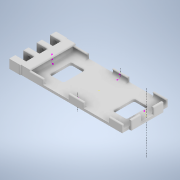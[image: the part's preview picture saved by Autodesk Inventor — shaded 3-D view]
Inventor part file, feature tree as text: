
AUTODESK INVENTOR PART (.ipt)
format: ipt  version: 2020 (Build 240168000, 168)  size: 727,040 bytes
history: native  units: mm
features: projected_geometry x18, sketch x14, extrude x12, other x3
ambient origin geometry x8: Origin, YZ Plane, XZ Plane, XY Plane, X Axis, Y Axis, Z Axis, Center Point
bodies: Solid1 (feature_tree)
feature tree (47):
  other  "Part9.1.ipt"
  extrude  "Extrusion1"  Depth=0.405517mm TaperAngle=0.0deg
  extrude  "Extrusion2"  Depth=15.5mm TaperAngle=0.0deg
  extrude  "Extrusion3"  Depth=20.0mm TaperAngle=0.0deg
  extrude  "Extrusion4"  Depth=40.0mm
  extrude  "Extrusion5"  Depth=12.0mm
  sketch  "Sketch10"  dims[d70=5.0mm d71=8.75mm]
  extrude  "Extrusion8"  Depth=8.75mm
  sketch  "Sketch22"  dims[d72=1.0mm d73=0.0mm d74=1.0mm d75=0.0mm]
  sketch  "Sketch23"  dims[d76=97.5mm d77=0.0mm d88=97.5mm d89=0.0mm]
  extrude  "Extrusion15"  Depth=1.0mm TaperAngle=0.0deg
  sketch  "Sketch27"  dims[d92=8.3mm d93=8.3mm]
  extrude  "Extrusion16"  Depth=97.5mm TaperAngle=0.0deg
  extrude  "Extrusion17"  Depth=17.25mm
  extrude  "Extrusion18"  Depth=8.3mm
  extrude  "Extrusion19"  Depth=12.8mm
  extrude  "Extrusion20"  Depth=9.591003mm
  other  "Solid2::Part9.1.ipt"
  other  "TaggingFeature1"
  sketch  "Sketch1"  dims[d0=0.405517mm d1=50.68mm d2=0.0mm]
  sketch  "Sketch3"  dims[d7=8.5mm d8=0.0mm d9=15.5mm d10=0.0mm]
  projected_geometry  "Projected Loop1"
  sketch  "Sketch5"  dims[d15=15.5mm d16=0.0mm d17=20.0mm d18=0.0mm]
  sketch  "Sketch6"  dims[d36=141.75mm d37=0.0mm d60=40.0mm]
  sketch  "Sketch7"  dims[d61=40.0mm d63=12.0mm]
  projected_geometry  "Projected Loop3"
  projected_geometry  "Projected Loop16"
  projected_geometry  "Projected Loop17"
  projected_geometry  "Projected Loop18"
  projected_geometry  "Projected Loop19"
  projected_geometry  "Projected Loop20"
  projected_geometry  "Projected Loop22"
  sketch  "Sketch26"  dims[d90=6.4mm d91=17.25mm]
  projected_geometry  "Projected Loop26"
  projected_geometry  "Projected Loop27"
  sketch  "Sketch28"  dims[d94=12.8mm d95=12.8mm]
  projected_geometry  "Projected Loop28"
  sketch  "Sketch29"  dims[d96=9.591003mm d98=9.591003mm]
  projected_geometry  "Projected Loop29"
  sketch  "Sketch30"  dims[d99=20.0mm]
  projected_geometry  "Projected Loop30"
  projected_geometry  "Projected Loop31"
  projected_geometry  "Projected Loop32"
  sketch  "Sketch31"  dims[d100=97.5mm d101=0.0mm d108=2.783mm d109=0.0mm d56=0.5mm d57=0.872665mm d58=0.5mm d59=0.872665mm d102=0.5mm d103=0.872665mm d104=0.5mm d105=0.872665mm]
  projected_geometry  "Projected Loop33"
  projected_geometry  "Projected Loop34"
  projected_geometry  "Projected Loop35"
